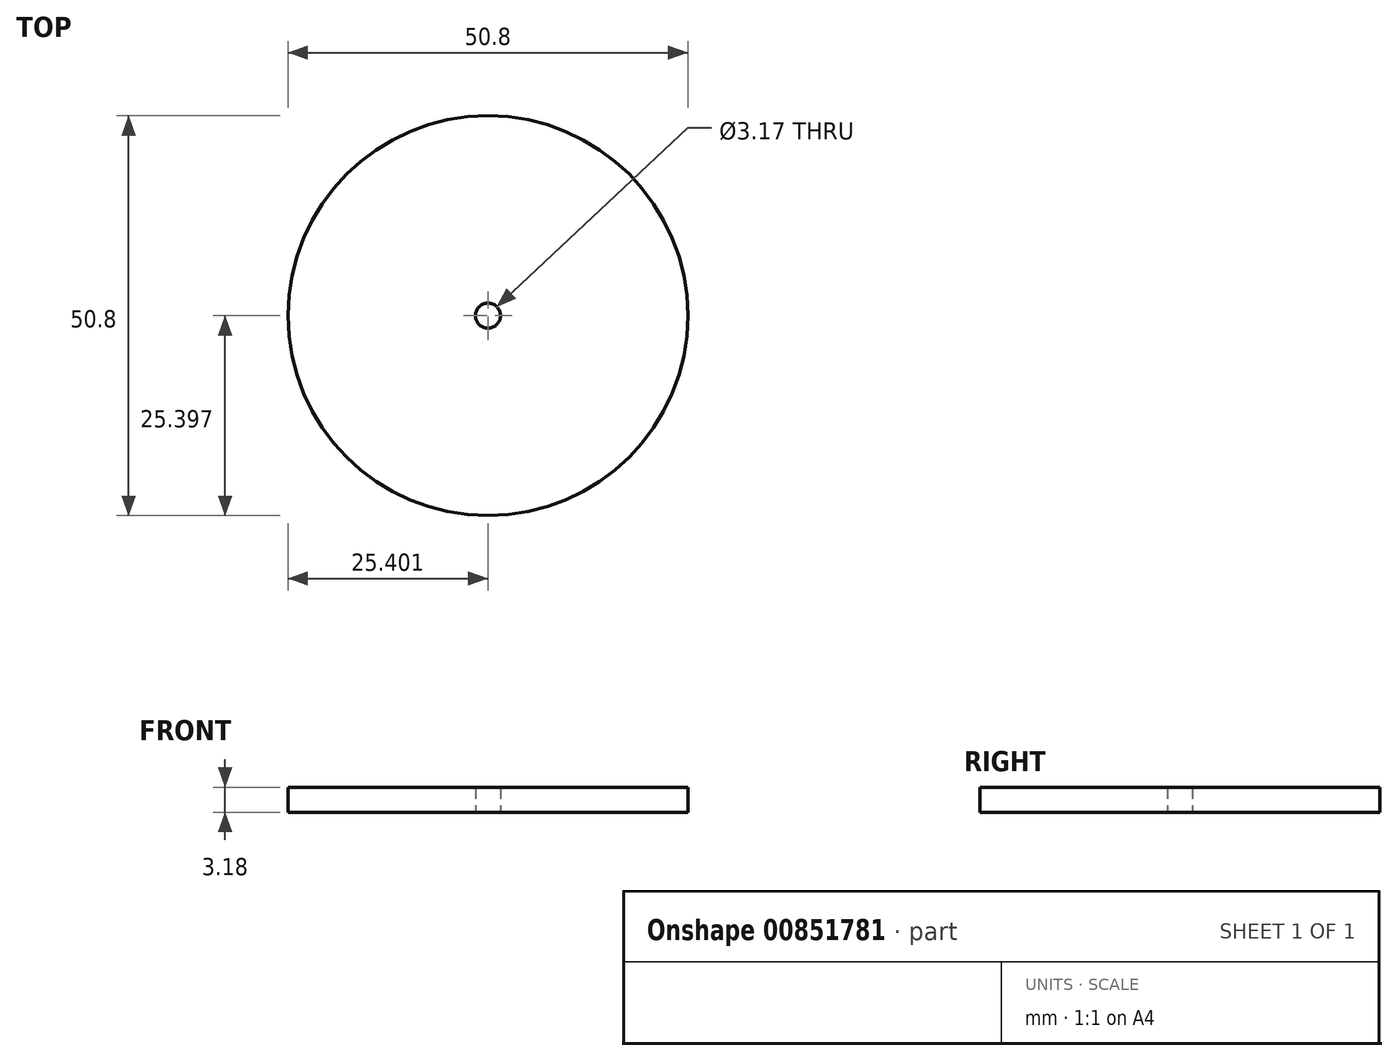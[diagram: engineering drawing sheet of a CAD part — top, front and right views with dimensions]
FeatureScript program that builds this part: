
annotation { "Feature Type Name" : "Feature", "Feature Type Description" : "" }
export const myFeature = defineFeature(function(context is Context, id is Id, definition is map)
    precondition{}
    {
        {
            var Q0;
            Q0=qCreatedBy(makeId("Top.planeOp"),FACE);
            var sketch = newSketch(context, id + "F0", { "sketchPlane" : qUnion([Q0])});
            skCircle(sketch, "E0", {"center": v(-0.25, 0.75) * mm, "radius": 25.4 * mm});
            skCircle(sketch, "E1", {"center": v(-0.25, 0.75) * mm, "radius": 1.59 * mm});
            skSolve(sketch);
        }
        {
            var Q0;
            Q0=makeQuery(id+"F0.imprint","IMPRINT",FACE,{"disambiguationData":[TD([[makeQuery(id+"F0.imprint","IMPRINT",EDGE,{"derivedFrom":sQuery(id+"F0.wireOp",EDGE,"E0")}),1.0]])]});
            extrude(context, id + "F1", {"entities" : qUnion([Q0]), "depth" : 3.17 * mm, "offsetDistance" : 25.4 * mm});
        }
    });
